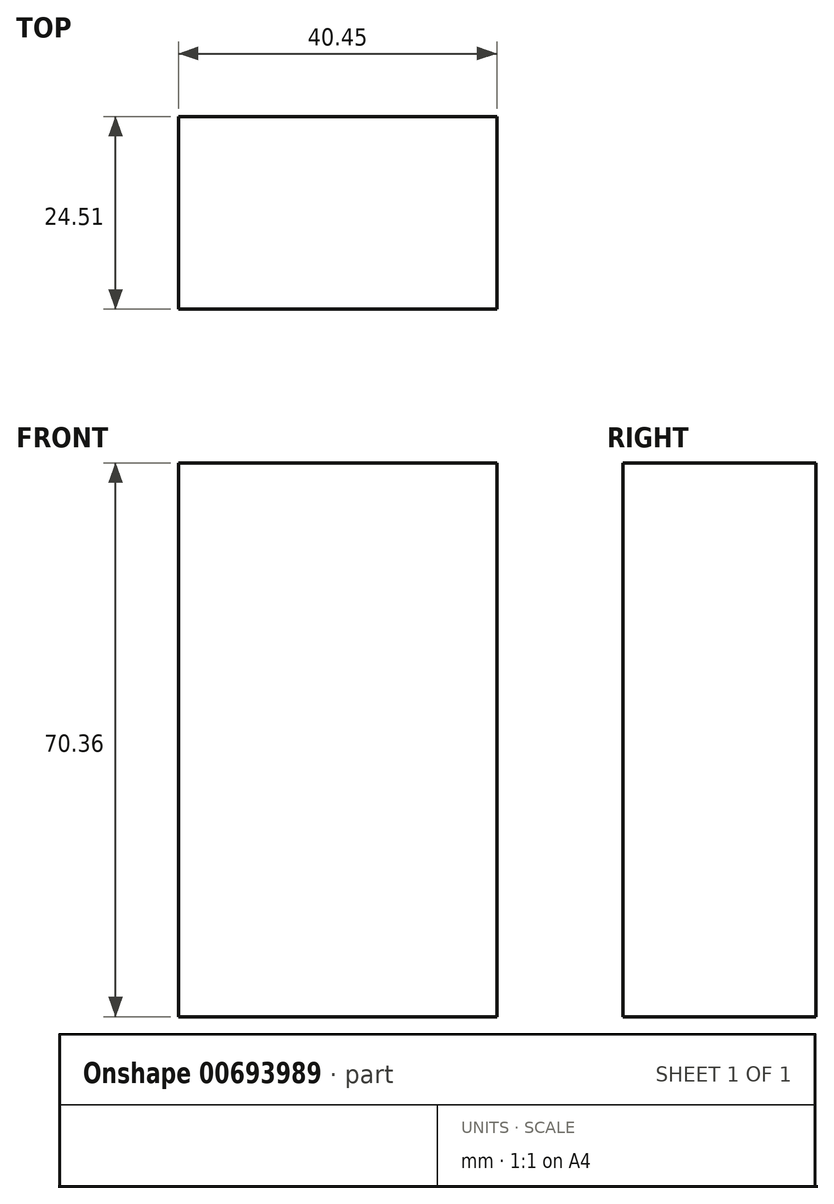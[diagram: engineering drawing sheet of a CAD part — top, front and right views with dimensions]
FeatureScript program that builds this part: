
annotation { "Feature Type Name" : "Feature", "Feature Type Description" : "" }
export const myFeature = defineFeature(function(context is Context, id is Id, definition is map)
    precondition{}
    {
        {
            var Q0;
            Q0=qCreatedBy(makeId("Top.planeOp"),FACE);
            var sketch = newSketch(context, id + "F0", { "sketchPlane" : qUnion([Q0])});
            skLineSegment(sketch, "E0.bottom", {"start": v(0.44, 0.44) * mm, "end": v(40.9, 0.44) * mm});
            skLineSegment(sketch, "E0.top", {"start": v(0.44, 24.95) * mm, "end": v(40.9, 24.95) * mm});
            skLineSegment(sketch, "E0.left", {"start": v(0.44, 0.44) * mm, "end": v(0.44, 24.95) * mm});
            skLineSegment(sketch, "E0.right", {"start": v(40.9, 0.44) * mm, "end": v(40.9, 24.95) * mm});
            skSolve(sketch);
        }
        {
            var Q0;
            Q0 = qSketchRegion(id + "F0", true);
            extrude(context, id + "F1", {"entities" : qUnion([Q0]), "depth" : 70.36 * mm, "offsetDistance" : 25.4 * mm});
        }
    });
